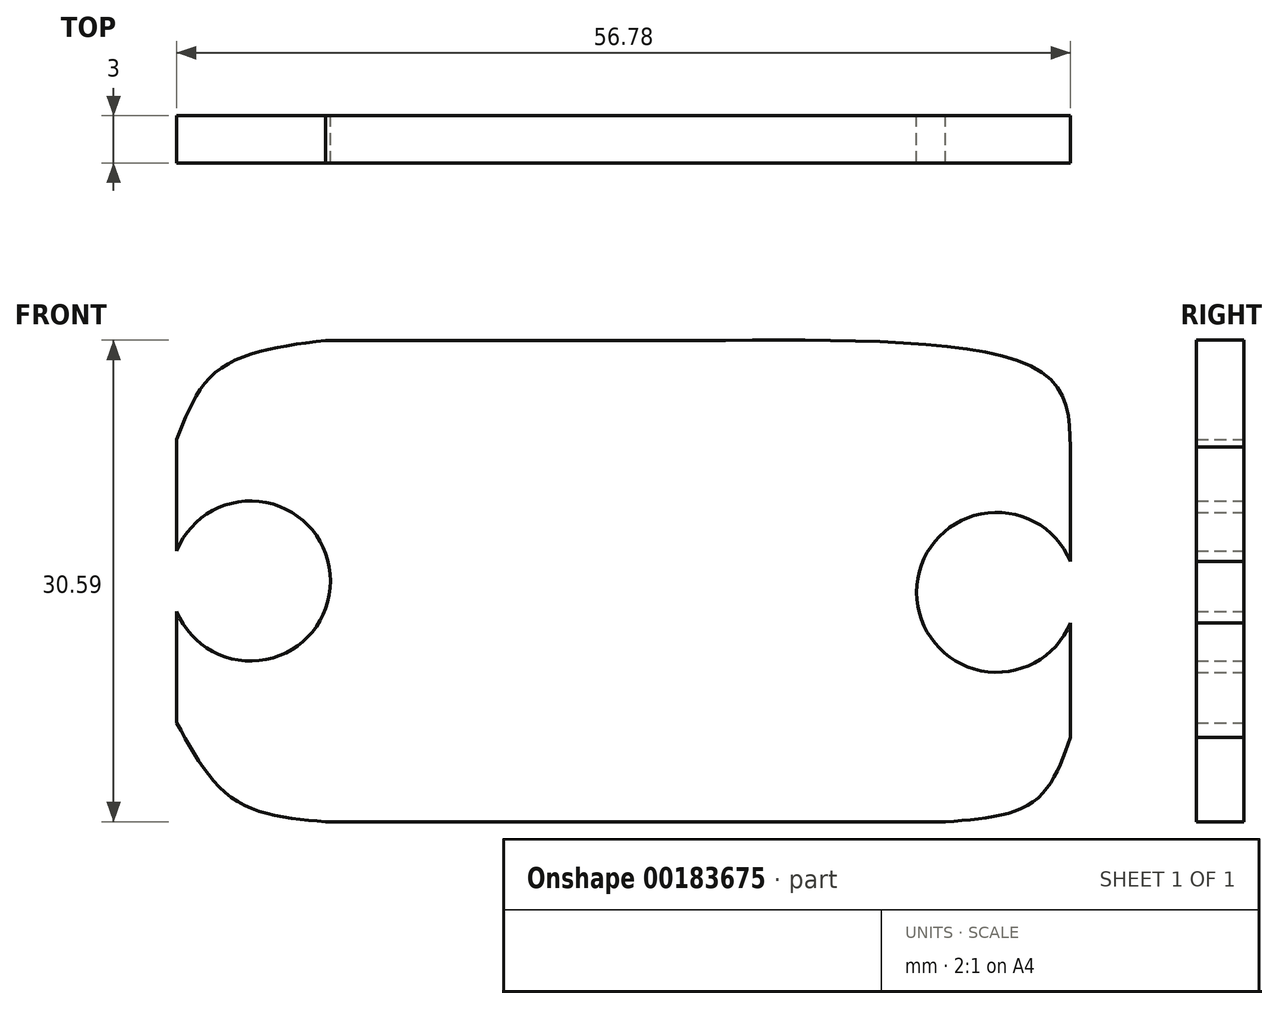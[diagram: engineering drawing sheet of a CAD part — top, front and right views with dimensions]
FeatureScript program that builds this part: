
annotation { "Feature Type Name" : "Feature", "Feature Type Description" : "" }
export const myFeature = defineFeature(function(context is Context, id is Id, definition is map)
    precondition{}
    {
        {
            var Q0;
            Q0=qCreatedBy(makeId("Front.planeOp"),FACE);
            var sketch = newSketch(context, id + "F0", { "sketchPlane" : qUnion([Q0])});
            skPoint(sketch, "E0.middle", {"position": v(0, 0) * mm});
            skArc(sketch, "E1", {"start": v(-41.57, 13.37) * mm, "mid": v(-31.79, 15.29) * mm, "end": v(-41.57, 17.21) * mm});
            skLineSegment(sketch, "E2", {"start": v(-41.57, 17.21) * mm, "end": v(-41.57, 24.29) * mm});
            skPoint(sketch, "E3.centerSnap0", {"position": v(-31.79, 15.29) * mm});
            skLineSegment(sketch, "E4", {"start": v(15.21, 12.58) * mm, "end": v(15.21, 12.58) * mm});
            skArc(sketch, "E5", {"start": v(15.21, 16.52) * mm, "mid": v(5.44, 14.57) * mm, "end": v(15.21, 12.63) * mm});
            skLineSegment(sketch, "E6", {"start": v(-6.7, 30.58) * mm, "end": v(-32.1, 30.58) * mm});
            skLineSegment(sketch, "E7", {"start": v(15.21, 16.52) * mm, "end": v(15.21, 23.8) * mm});
            skLineSegment(sketch, "E8", {"start": v(7.27, 0) * mm, "end": v(-32.1, 0) * mm});
            skLineSegment(sketch, "E9", {"start": v(15.21, 5.34) * mm, "end": v(15.21, 12.63) * mm});
            skLineSegment(sketch, "E10", {"start": v(-41.57, 6.29) * mm, "end": v(-41.57, 13.37) * mm});
            skFitSpline(sketch, "E11", {"points": [v(-41.57, 6.29) * mm, v(-37.85, 1.39) * mm, v(-32.1, 0) * mm], "startDerivative": vector(6.29, -11.46) * mm, "endDerivative": vector(12.69, -1.09) * mm});
            skFitSpline(sketch, "E12", {"points": [v(15.21, 5.34) * mm, v(12.87, 1.29) * mm, v(7.27, 0) * mm], "startDerivative": vector(-3.6, -10) * mm, "endDerivative": vector(-12.15, -0.85) * mm});
            skFitSpline(sketch, "E13", {"points": [v(-41.57, 24.29) * mm, v(-38.87, 28.71) * mm, v(-32.1, 30.58) * mm], "startDerivative": vector(4.28, 10.98) * mm, "endDerivative": vector(14.42, 1.83) * mm});
            skFitSpline(sketch, "E14", {"points": [v(15.21, 23.8) * mm, v(13.7, 28.32) * mm, v(-6.7, 30.58) * mm], "startDerivative": vector(-0.48, 15.6) * mm, "endDerivative": vector(-38.85, -0.2) * mm});
            skSolve(sketch);
        }
        {
            var Q0;
            Q0 = qSketchRegion(id + "F0", true);
            extrude(context, id + "F1", {"entities" : qUnion([Q0]), "depth" : 3 * mm});
        }
    });
